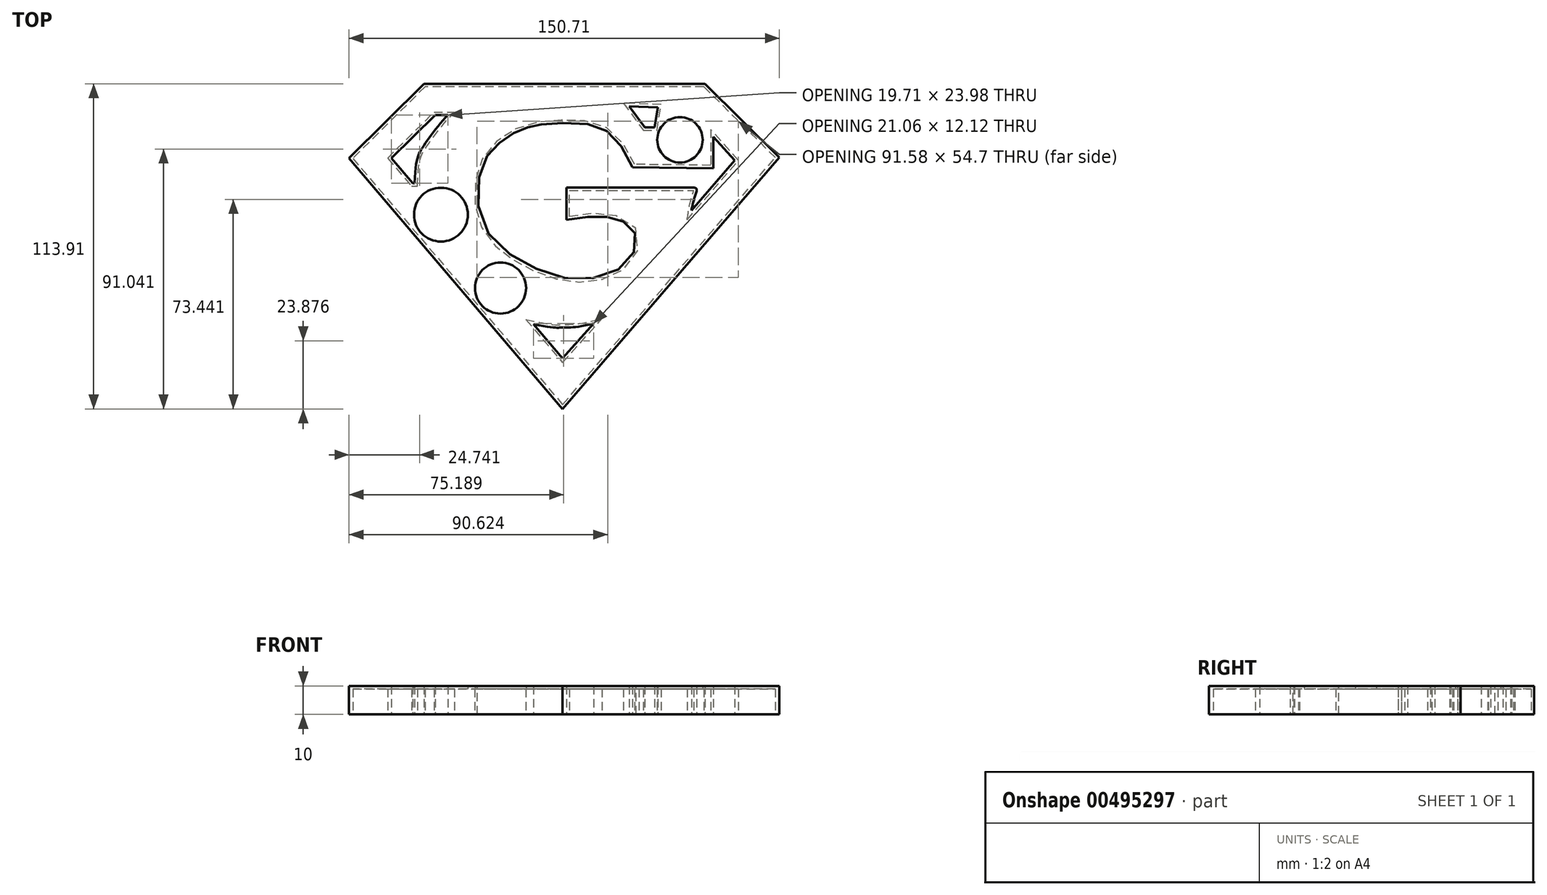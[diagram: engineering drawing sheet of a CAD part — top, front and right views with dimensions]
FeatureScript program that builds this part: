
annotation { "Feature Type Name" : "Feature", "Feature Type Description" : "" }
export const myFeature = defineFeature(function(context is Context, id is Id, definition is map)
    precondition{}
    {
        {
            var Q0;
            Q0=qCreatedBy(makeId("Top.planeOp"),FACE);
            var sketch = newSketch(context, id + "F0", { "sketchPlane" : qUnion([Q0])});
            skLineSegment(sketch, "E0", {"start": v(-74.83, 17.46) * mm, "end": v(0, -70.4) * mm});
            skLineSegment(sketch, "E1", {"start": v(0, -70.4) * mm, "end": v(75.88, 17.75) * mm});
            skLineSegment(sketch, "E2", {"start": v(75.88, 17.75) * mm, "end": v(49.86, 43.52) * mm});
            skLineSegment(sketch, "E3", {"start": v(49.86, 43.52) * mm, "end": v(-48.56, 43.52) * mm});
            skLineSegment(sketch, "E4", {"start": v(-48.56, 43.52) * mm, "end": v(-74.83, 17.46) * mm});
            skLineSegment(sketch, "E5", {"start": v(-59.94, 17.46) * mm, "end": v(-44.64, 32.64) * mm});
            skLineSegment(sketch, "E6", {"start": v(-44.64, 32.64) * mm, "end": v(-40.24, 32.64) * mm});
            skLineSegment(sketch, "E7", {"start": v(-59.94, 17.46) * mm, "end": v(-52.45, 8.66) * mm});
            skLineSegment(sketch, "E8", {"start": v(-52.45, 8.66) * mm, "end": v(-51.82, 8.66) * mm});
            skFitSpline(sketch, "E9", {"points": [v(-51.82, 8.66) * mm, v(-49.01, 21.3) * mm, v(-40.24, 32.64) * mm], "startDerivative": vector(2.11, 50.89) * mm, "endDerivative": vector(20.03, 21.12) * mm});
            skFitSpline(sketch, "E10", {"points": [v(24.51, 14.3) * mm, v(17.32, 25.5) * mm, v(8.15, 29.46) * mm, v(-6.49, 29.38) * mm, v(-11.6, 28.42) * mm, v(-17, 26.34) * mm, v(-23.1, 22.05) * mm, v(-28.35, 14.3) * mm, v(-27.93, -5.35) * mm, v(-11.88, -20.02) * mm, v(8.46, -24.86) * mm, v(23.68, -17.8) * mm, v(25.2, -8.53) * mm, v(20.08, -4.24) * mm, v(12.33, -2.86) * mm, v(1.4, -4.1) * mm], "startDerivative": vector(-78.23, 181.81) * mm, "endDerivative": vector(-173.23, -28.5) * mm});
            skLineSegment(sketch, "E11", {"start": v(1.4, -4.1) * mm, "end": v(1.4, 7.14) * mm});
            skLineSegment(sketch, "E12", {"start": v(1.4, 7.14) * mm, "end": v(46, 7.14) * mm});
            skLineSegment(sketch, "E13", {"start": v(45.15, -0.78) * mm, "end": v(60.25, 16.73) * mm});
            skLineSegment(sketch, "E14", {"start": v(60.25, 16.73) * mm, "end": v(52.84, 24.93) * mm});
            skLineSegment(sketch, "E15", {"start": v(52.84, 24.93) * mm, "end": v(52.84, 13.98) * mm});
            skLineSegment(sketch, "E16", {"start": v(52.84, 13.98) * mm, "end": v(24.51, 14.3) * mm});
            skFitSpline(sketch, "E17", {"points": [v(45.15, -0.78) * mm, v(46.58, 4.8) * mm, v(46, 7.14) * mm], "startDerivative": vector(1.7, 10.85) * mm, "endDerivative": vector(-10.2, 0) * mm});
            skLineSegment(sketch, "E18", {"start": v(-10.17, -40.64) * mm, "end": v(0, -52.58) * mm});
            skLineSegment(sketch, "E19", {"start": v(0, -52.58) * mm, "end": v(10.89, -40.45) * mm});
            skFitSpline(sketch, "E20", {"points": [v(-10.17, -40.64) * mm, v(0, -41.84) * mm, v(10.89, -40.45) * mm], "startDerivative": vector(46.45, -9.9) * mm, "endDerivative": vector(37.05, 9.51) * mm});
            skLineSegment(sketch, "E21", {"start": v(23.33, 35.69) * mm, "end": v(28.75, 28.3) * mm});
            skLineSegment(sketch, "E22", {"start": v(28.75, 28.3) * mm, "end": v(32.2, 28.3) * mm});
            skLineSegment(sketch, "E23", {"start": v(32.2, 28.3) * mm, "end": v(33.31, 35.32) * mm});
            skLineSegment(sketch, "E24", {"start": v(33.31, 35.32) * mm, "end": v(23.33, 35.69) * mm});
            skCircle(sketch, "E25", {"center": v(-42.63, -2.3) * mm, "radius": 8.42 * mm});
            skCircle(sketch, "E26", {"center": v(-21.76, -28.03) * mm, "radius": 7.95 * mm});
            skCircle(sketch, "E27", {"center": v(41.1, 23.9) * mm, "radius": 6.95 * mm});
            skSolve(sketch);
        }
        {
            var Q0;
            Q0=qSketchRegion(id+"F0",true);
            extrude(context, id + "F1", {"entities" : qUnion([Q0]), "depth" : 10 * mm});
        }
        {
            var Q0;
            Q0=makeQuery(id+"F1.opExtrude","CAP_FACE",FACE,{"disambiguationData":[OSD([sQuery(id+"F0.wireOp",EDGE,"E0"),sQuery(id+"F0.wireOp",EDGE,"E1"),sQuery(id+"F0.wireOp",EDGE,"E2"),sQuery(id+"F0.wireOp",EDGE,"E3"),sQuery(id+"F0.wireOp",EDGE,"E4"),sQuery(id+"F0.wireOp",EDGE,"E5"),sQuery(id+"F0.wireOp",EDGE,"E6"),sQuery(id+"F0.wireOp",EDGE,"E7"),sQuery(id+"F0.wireOp",EDGE,"E8"),sQuery(id+"F0.wireOp",EDGE,"E9"),sQuery(id+"F0.wireOp",EDGE,"E10"),sQuery(id+"F0.wireOp",EDGE,"E11"),sQuery(id+"F0.wireOp",EDGE,"E12"),sQuery(id+"F0.wireOp",EDGE,"E13"),sQuery(id+"F0.wireOp",EDGE,"E14"),sQuery(id+"F0.wireOp",EDGE,"E15"),sQuery(id+"F0.wireOp",EDGE,"E16"),sQuery(id+"F0.wireOp",EDGE,"E17"),sQuery(id+"F0.wireOp",EDGE,"E18"),sQuery(id+"F0.wireOp",EDGE,"E19"),sQuery(id+"F0.wireOp",EDGE,"E20"),sQuery(id+"F0.wireOp",EDGE,"E21"),sQuery(id+"F0.wireOp",EDGE,"E22"),sQuery(id+"F0.wireOp",EDGE,"E23"),sQuery(id+"F0.wireOp",EDGE,"E24")])],"isStart":true});
            shell(context, id + "F2", {"entities" : qUnion([Q0]), "thickness" : 1 * mm});
        }
        {
            var Q0;
            {var subQ0=sQuery(id+"F0.wireOp",EDGE,"E27");var subQ1=sQuery(id+"F0.wireOp",EDGE,"E26");var subQ2=sQuery(id+"F0.wireOp",EDGE,"E25");var subQ3=sQuery(id+"F0.wireOp",EDGE,"E24");var subQ4=sQuery(id+"F0.wireOp",EDGE,"E23");var subQ5=sQuery(id+"F0.wireOp",EDGE,"E22");var subQ6=sQuery(id+"F0.wireOp",EDGE,"E21");var subQ7=sQuery(id+"F0.wireOp",EDGE,"E20");var subQ8=sQuery(id+"F0.wireOp",EDGE,"E19");var subQ9=sQuery(id+"F0.wireOp",EDGE,"E18");var subQ10=sQuery(id+"F0.wireOp",EDGE,"E17");var subQ11=sQuery(id+"F0.wireOp",EDGE,"E16");var subQ12=sQuery(id+"F0.wireOp",EDGE,"E15");var subQ13=sQuery(id+"F0.wireOp",EDGE,"E14");var subQ14=sQuery(id+"F0.wireOp",EDGE,"E13");var subQ15=sQuery(id+"F0.wireOp",EDGE,"E12");var subQ16=sQuery(id+"F0.wireOp",EDGE,"E11");var subQ17=sQuery(id+"F0.wireOp",EDGE,"E10");var subQ18=sQuery(id+"F0.wireOp",EDGE,"E9");var subQ19=sQuery(id+"F0.wireOp",EDGE,"E8");var subQ20=sQuery(id+"F0.wireOp",EDGE,"E7");var subQ21=sQuery(id+"F0.wireOp",EDGE,"E6");var subQ22=sQuery(id+"F0.wireOp",EDGE,"E5");var subQ23=sQuery(id+"F0.wireOp",EDGE,"E4");var subQ24=sQuery(id+"F0.wireOp",EDGE,"E3");var subQ25=sQuery(id+"F0.wireOp",EDGE,"E2");var subQ26=sQuery(id+"F0.wireOp",EDGE,"E1");var subQ27=sQuery(id+"F0.wireOp",EDGE,"E0");Q0=makeQuery(id+"F2.opShell","OFFSET_FACE",FACE,{"disambiguationData":[OSD([subQ27,subQ26,subQ25,subQ24,subQ23,subQ22,subQ21,subQ20,subQ19,subQ18,subQ17,subQ16,subQ15,subQ14,subQ13,subQ12,subQ11,subQ10,subQ9,subQ8,subQ7,subQ6,subQ5,subQ4,subQ3,subQ2,subQ1,subQ0]),TDD([makeQuery(id+"F1.opExtrude","CAP_FACE",FACE,{"disambiguationData":[OSD([subQ27,subQ26,subQ25,subQ24,subQ23,subQ22,subQ21,subQ20,subQ19,subQ18,subQ17,subQ16,subQ15,subQ14,subQ13,subQ12,subQ11,subQ10,subQ9,subQ8,subQ7,subQ6,subQ5,subQ4,subQ3,subQ2,subQ1,subQ0])],"isStart":true})]),OD(4.0)]});}
            var Q1;
            {var subQ0=sQuery(id+"F0.wireOp",EDGE,"E27");var subQ1=sQuery(id+"F0.wireOp",EDGE,"E26");var subQ2=sQuery(id+"F0.wireOp",EDGE,"E25");var subQ3=sQuery(id+"F0.wireOp",EDGE,"E24");var subQ4=sQuery(id+"F0.wireOp",EDGE,"E23");var subQ5=sQuery(id+"F0.wireOp",EDGE,"E22");var subQ6=sQuery(id+"F0.wireOp",EDGE,"E21");var subQ7=sQuery(id+"F0.wireOp",EDGE,"E20");var subQ8=sQuery(id+"F0.wireOp",EDGE,"E19");var subQ9=sQuery(id+"F0.wireOp",EDGE,"E18");var subQ10=sQuery(id+"F0.wireOp",EDGE,"E17");var subQ11=sQuery(id+"F0.wireOp",EDGE,"E16");var subQ12=sQuery(id+"F0.wireOp",EDGE,"E15");var subQ13=sQuery(id+"F0.wireOp",EDGE,"E14");var subQ14=sQuery(id+"F0.wireOp",EDGE,"E13");var subQ15=sQuery(id+"F0.wireOp",EDGE,"E12");var subQ16=sQuery(id+"F0.wireOp",EDGE,"E11");var subQ17=sQuery(id+"F0.wireOp",EDGE,"E10");var subQ18=sQuery(id+"F0.wireOp",EDGE,"E9");var subQ19=sQuery(id+"F0.wireOp",EDGE,"E8");var subQ20=sQuery(id+"F0.wireOp",EDGE,"E7");var subQ21=sQuery(id+"F0.wireOp",EDGE,"E6");var subQ22=sQuery(id+"F0.wireOp",EDGE,"E5");var subQ23=sQuery(id+"F0.wireOp",EDGE,"E4");var subQ24=sQuery(id+"F0.wireOp",EDGE,"E3");var subQ25=sQuery(id+"F0.wireOp",EDGE,"E2");var subQ26=sQuery(id+"F0.wireOp",EDGE,"E1");var subQ27=sQuery(id+"F0.wireOp",EDGE,"E0");Q1=makeQuery(id+"F2.opShell","OFFSET_FACE",FACE,{"disambiguationData":[OSD([subQ27,subQ26,subQ25,subQ24,subQ23,subQ22,subQ21,subQ20,subQ19,subQ18,subQ17,subQ16,subQ15,subQ14,subQ13,subQ12,subQ11,subQ10,subQ9,subQ8,subQ7,subQ6,subQ5,subQ4,subQ3,subQ2,subQ1,subQ0]),TDD([makeQuery(id+"F1.opExtrude","CAP_FACE",FACE,{"disambiguationData":[OSD([subQ27,subQ26,subQ25,subQ24,subQ23,subQ22,subQ21,subQ20,subQ19,subQ18,subQ17,subQ16,subQ15,subQ14,subQ13,subQ12,subQ11,subQ10,subQ9,subQ8,subQ7,subQ6,subQ5,subQ4,subQ3,subQ2,subQ1,subQ0])],"isStart":true})]),OD(5.0)]});}
            var Q2;
            {var subQ0=sQuery(id+"F0.wireOp",EDGE,"E27");var subQ1=sQuery(id+"F0.wireOp",EDGE,"E26");var subQ2=sQuery(id+"F0.wireOp",EDGE,"E25");var subQ3=sQuery(id+"F0.wireOp",EDGE,"E24");var subQ4=sQuery(id+"F0.wireOp",EDGE,"E23");var subQ5=sQuery(id+"F0.wireOp",EDGE,"E22");var subQ6=sQuery(id+"F0.wireOp",EDGE,"E21");var subQ7=sQuery(id+"F0.wireOp",EDGE,"E20");var subQ8=sQuery(id+"F0.wireOp",EDGE,"E19");var subQ9=sQuery(id+"F0.wireOp",EDGE,"E18");var subQ10=sQuery(id+"F0.wireOp",EDGE,"E17");var subQ11=sQuery(id+"F0.wireOp",EDGE,"E16");var subQ12=sQuery(id+"F0.wireOp",EDGE,"E15");var subQ13=sQuery(id+"F0.wireOp",EDGE,"E14");var subQ14=sQuery(id+"F0.wireOp",EDGE,"E13");var subQ15=sQuery(id+"F0.wireOp",EDGE,"E12");var subQ16=sQuery(id+"F0.wireOp",EDGE,"E11");var subQ17=sQuery(id+"F0.wireOp",EDGE,"E10");var subQ18=sQuery(id+"F0.wireOp",EDGE,"E9");var subQ19=sQuery(id+"F0.wireOp",EDGE,"E8");var subQ20=sQuery(id+"F0.wireOp",EDGE,"E7");var subQ21=sQuery(id+"F0.wireOp",EDGE,"E6");var subQ22=sQuery(id+"F0.wireOp",EDGE,"E5");var subQ23=sQuery(id+"F0.wireOp",EDGE,"E4");var subQ24=sQuery(id+"F0.wireOp",EDGE,"E3");var subQ25=sQuery(id+"F0.wireOp",EDGE,"E2");var subQ26=sQuery(id+"F0.wireOp",EDGE,"E1");var subQ27=sQuery(id+"F0.wireOp",EDGE,"E0");Q2=makeQuery(id+"F2.opShell","OFFSET_FACE",FACE,{"disambiguationData":[OSD([subQ27,subQ26,subQ25,subQ24,subQ23,subQ22,subQ21,subQ20,subQ19,subQ18,subQ17,subQ16,subQ15,subQ14,subQ13,subQ12,subQ11,subQ10,subQ9,subQ8,subQ7,subQ6,subQ5,subQ4,subQ3,subQ2,subQ1,subQ0]),TDD([makeQuery(id+"F1.opExtrude","CAP_FACE",FACE,{"disambiguationData":[OSD([subQ27,subQ26,subQ25,subQ24,subQ23,subQ22,subQ21,subQ20,subQ19,subQ18,subQ17,subQ16,subQ15,subQ14,subQ13,subQ12,subQ11,subQ10,subQ9,subQ8,subQ7,subQ6,subQ5,subQ4,subQ3,subQ2,subQ1,subQ0])],"isStart":true})]),OD(6.0)]});}
            extrude(context, id + "F3", {"entities" : qUnion([Q0, Q1, Q2]), "operationType" : NewBodyOperationType.REMOVE, "oppositeDirection" : true, "depth" : 105.3 * mm});
        }
    });
